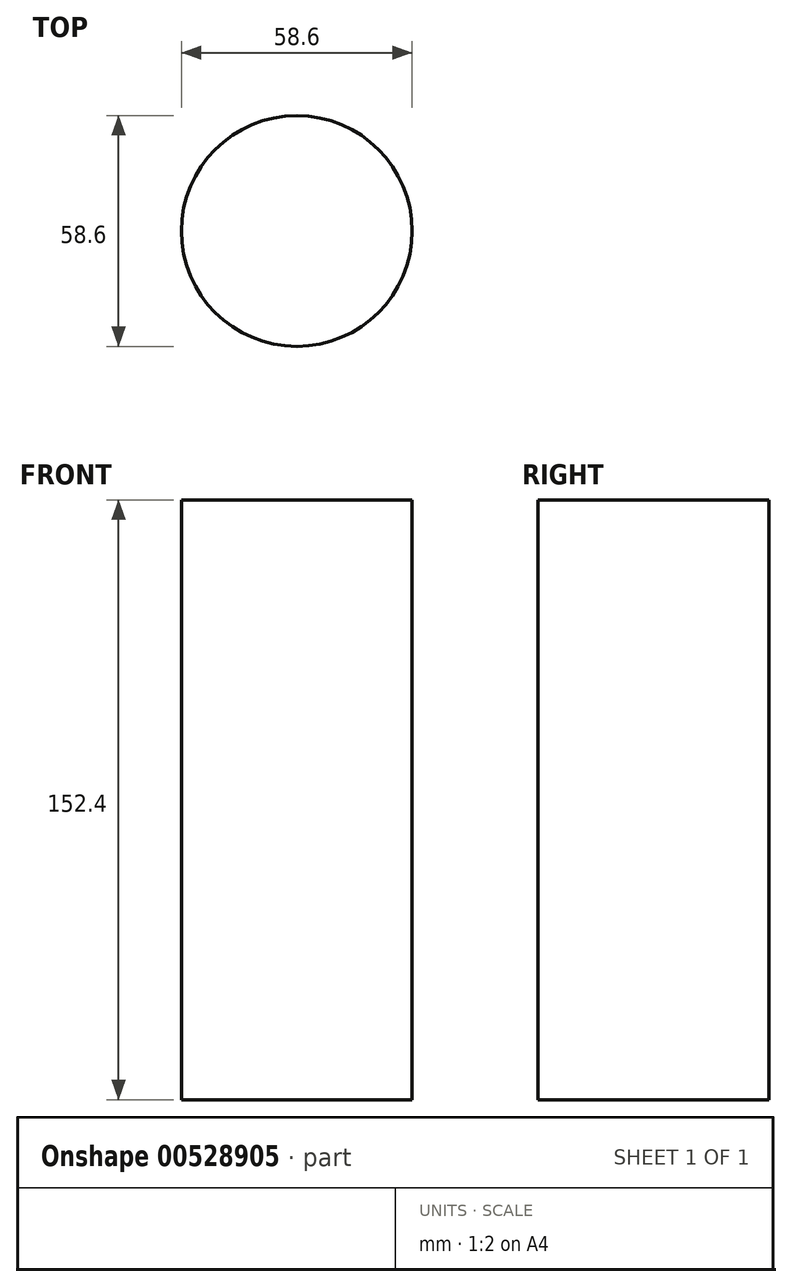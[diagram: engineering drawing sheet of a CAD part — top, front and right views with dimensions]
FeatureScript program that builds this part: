
annotation { "Feature Type Name" : "Feature", "Feature Type Description" : "" }
export const myFeature = defineFeature(function(context is Context, id is Id, definition is map)
    precondition{}
    {
        {
            var Q0;
            Q0=qCreatedBy(makeId("Top.planeOp"),FACE);
            var sketch = newSketch(context, id + "F0", { "sketchPlane" : qUnion([Q0])});
            skCircle(sketch, "E0", {"center": v(0, 0) * mm, "radius": 29.3 * mm});
            skSolve(sketch);
        }
        {
            var Q0;
            Q0 = qSketchRegion(id + "F0", true);
            extrude(context, id + "F1", {"entities" : qUnion([Q0]), "endBound" : BoundingType.SYMMETRIC, "depth" : 152.4 * mm, "offsetDistance" : 30.48 * mm});
        }
    });
